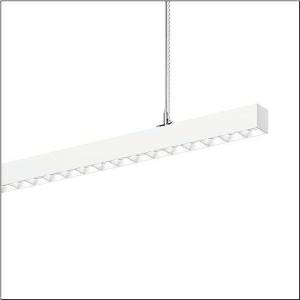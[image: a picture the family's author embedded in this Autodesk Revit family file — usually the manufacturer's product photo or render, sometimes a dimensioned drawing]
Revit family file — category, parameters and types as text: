
# Revit family: silica_21_51mx35da47wb
name_source: partatom
category: Lighting Fixtures
units: mm (PartAtom-declared; Revit-internal decimal feet)

## family parameters
Cut with Voids When Loaded = No
Host = Face
Light Source = No
Part Type = Normal
Room Calculation Point = No
Round Connector Dimension = Use Diameter
Shared = No

## types (1)
- --- (1 x LED, 7080 lm, 40.6 W, 4000K)
    Apparent Load = 41 VA
    CIE Flux Codes = 84 98 100 61 100
    Color Rendering = 80
    Color Temperature = 4000K
    Default Elevation = 1800 mm
    Description = Silica 21, office luminaire, primary light control with darklight reflector, of PMMA, white, CAT 2 (L<= 3000cd/m²), light emission: direct/indirect distribution, primary light characteristic: symmetric, installation type: suspended mounting, LED, rated luminous flux: 7.080lm, luminous efficacy: 174lm/W, light colour: 840, colour temperature: 4000K, control gear: DALI 2, with terminal, 3+2-pole, max. 2.5mm², mains connection: 220..240V, AC, 50/60Hz, rated input power: 40.6W, luminaire housing, of aluminium, traffic white (RAL 9016), length: 1.204mm, width: 53mm, height: 53mm, protection rating (complete): IP20, insulation class (complete): insulation class I (protective earthing), certification: CE, permissible operating ambient temperature: 0..+35°C, standard: EN 50419, packaging unit: 1 piece
    Height = 53 mm
    Lamp = 1 x LED
    Lamp Light Flux = 7080 lm
    Lamp Power = 40.6 W
    Lamp count = 1
    Length = 1204 mm
    Luminous efficacy = 174 lm/W
    Manufacturer = Siteco
    ModVariant = No
    Model = 51MX35DA47WB
    Mounting Place = Ceiling
    Mounting Type = Pendant
    Number of Poles = 1
    OnlyDefault = Yes
    Power Factor = 1
    Product Name = Silica 21
    Product group = office luminaire | ceiling pendant
    ProductGroupID = 903
    Protection Class = Protection class I
    Protection Degree = IP 20
    RLX_Detail_Level = 1
    RLX_Emergency_Light_Flux = 0 lm
    RLX_Emergency_Type = 0
    RLX_Emergency_Type_DB = No
    RlxData = <blob elided: 41001 chars, md5=813474d8>
    Socket = socket
    Standby Power = 0 W
    System Light Flux = 7080 lm
    System Power = 41 W
    Type Comments = factory setting: luminous flux: 100 % | dim-lin: 254 | 339 mA
    Type Image = l_1335921.jpg
    URL = http://relux.com
    VarID = @adj_120681
    Voltage = 0 V
    Weight = 0.00 kg
    Width = 53 mm

## geometry (parser evidence)
native form markers: Blend x4, Sweep x11
no freeform markers — native parametric forms only
